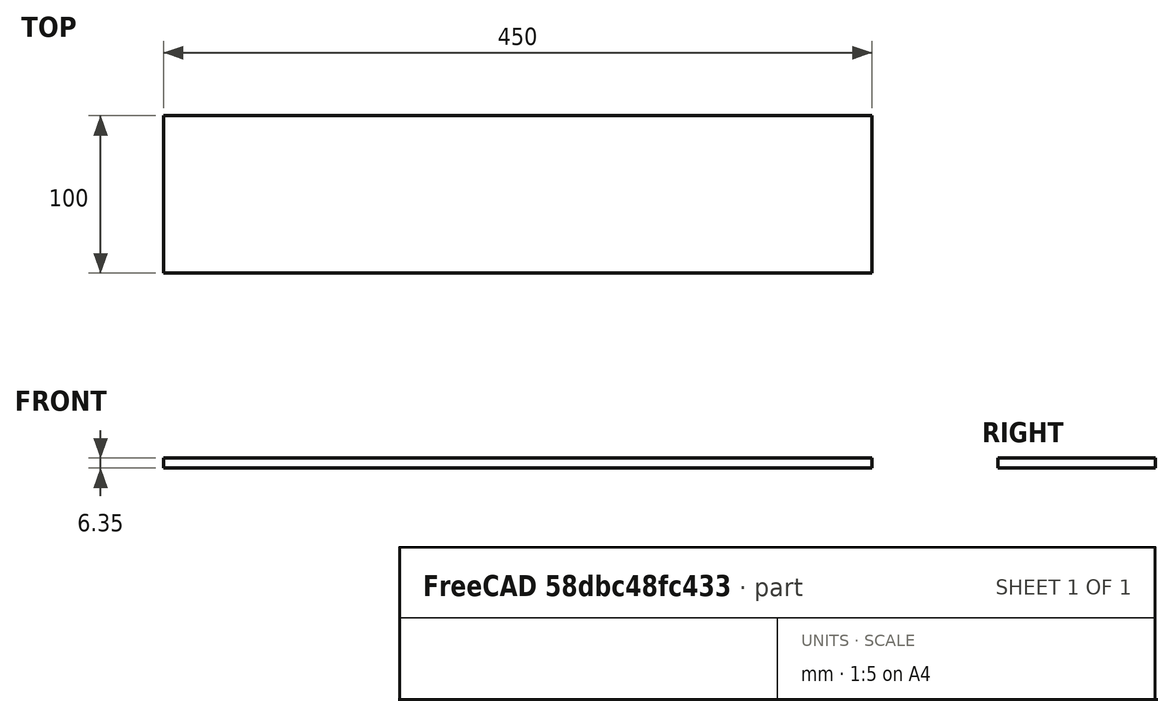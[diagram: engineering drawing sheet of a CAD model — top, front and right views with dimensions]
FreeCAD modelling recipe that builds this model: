
FCSTD DOCUMENT  (FreeCAD 0.16RUnknown)
Label: Laterales
License: All rights reserved
LicenseURL: http://berserk.design
objects: Sketcher::SketchObject×1, PartDesign::Pad×1
note: 3 computed .brp shape members not serialized (recipe doc carries the construction recipe); baked Part::Feature solids carry a one-line shape summary decoded from their .brp

FEATURE [Sketcher::SketchObject] Sketch
  sketch-geometry (4):
    g0: LineSegment StartX=0 StartY=0 StartZ=0 EndX=450 EndY=0 EndZ=0
    g1: LineSegment StartX=450 StartY=0 StartZ=0 EndX=450 EndY=100 EndZ=0
    g2: LineSegment StartX=450 StartY=100 StartZ=0 EndX=0 EndY=100 EndZ=0
    g3: LineSegment StartX=0 StartY=100 StartZ=0 EndX=0 EndY=0 EndZ=0
  constraints (11):
    c: Coincident(g0,g1)
    c: Coincident(g1,g2)
    c: Coincident(g2,g3)
    c: Coincident(g3,g0)
    c: Horizontal(g0)
    c: Horizontal(g2)
    c: Vertical(g1)
    c: Vertical(g3)
    c: Coincident(g0,g-1)
    c: DistanceX(g2,g2) = 450
    c: DistanceY(g3,g3) = 100
FEATURE [PartDesign::Pad] Pad
  Length = 6.35
  Length2 = 100
  Sketch = -> Sketch
  Type = 0
